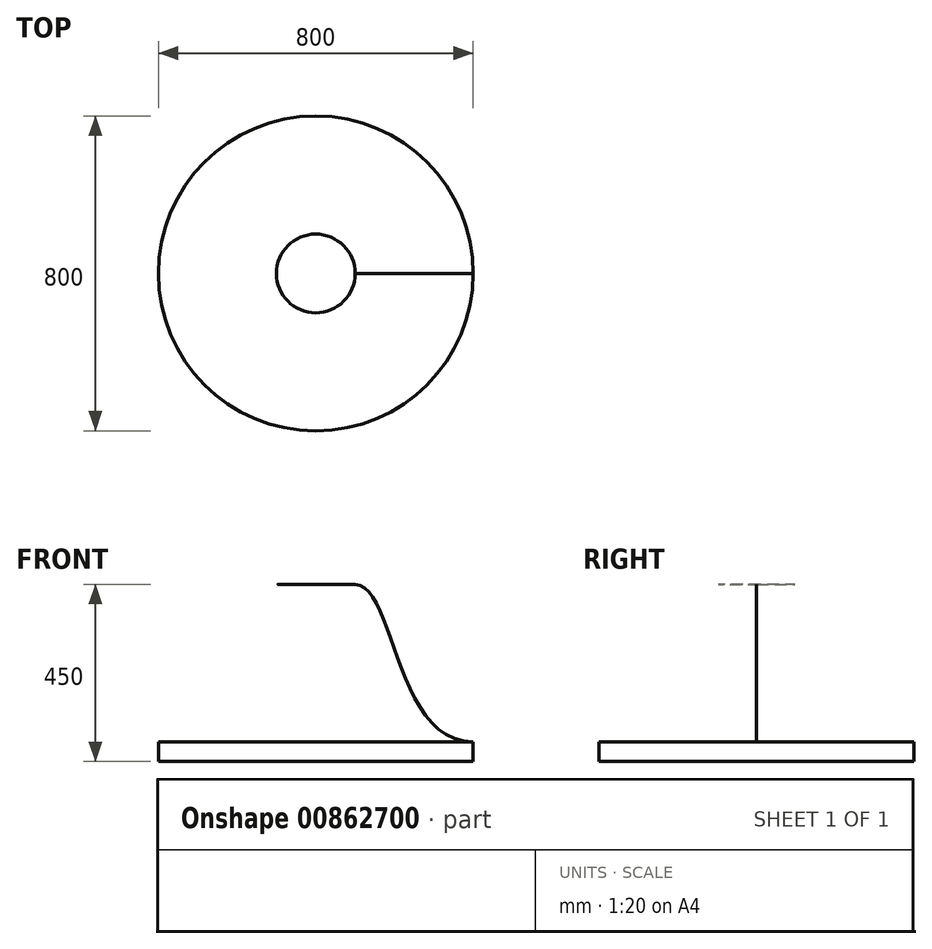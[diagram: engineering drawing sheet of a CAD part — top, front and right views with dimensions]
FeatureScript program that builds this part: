
annotation { "Feature Type Name" : "Feature", "Feature Type Description" : "" }
export const myFeature = defineFeature(function(context is Context, id is Id, definition is map)
    precondition{}
    {
        {
            var Q0;
            Q0=qCreatedBy(makeId("Top.planeOp"),FACE);
            var sketch = newSketch(context, id + "F0", { "sketchPlane" : qUnion([Q0])});
            skCircle(sketch, "E0", {"center": v(0, 0) * mm, "radius": 400 * mm});
            skSolve(sketch);
        }
        {
            var Q0;
            Q0=makeQuery(id+"F0.imprint","IMPRINT",FACE,{"disambiguationData":[TD([[makeQuery(id+"F0.imprint","IMPRINT",EDGE,{"derivedFrom":sQuery(id+"F0.wireOp",EDGE,"E0")}),1.0]])]});
            cPlane(context, id + "F1", {"entities" : qUnion([Q0]), "cplaneType" : CPlaneType.OFFSET, "offset" : 400 * mm, "width" : 150 * mm, "height" : 150 * mm});
        }
        {
            var Q0;
            Q0=qCreatedBy(id+"F1.planeOp",FACE);
            var sketch = newSketch(context, id + "F2", { "sketchPlane" : qUnion([Q0])});
            skCircle(sketch, "E1", {"center": v(0, 0) * mm, "radius": 100 * mm});
            skSolve(sketch);
        }
        {
            var Q0;
            Q0=makeQuery(id+"F0.imprint","IMPRINT",FACE,{"disambiguationData":[TD([[makeQuery(id+"F0.imprint","IMPRINT",EDGE,{"derivedFrom":sQuery(id+"F0.wireOp",EDGE,"E0")}),1.0]])]});
            var Q1;
            Q1=makeQuery(id+"F2.imprint","IMPRINT",FACE,{"disambiguationData":[TD([[makeQuery(id+"F2.imprint","IMPRINT",EDGE,{"derivedFrom":sQuery(id+"F2.wireOp",EDGE,"E1")}),1.0]])]});
            loft(context, id + "F3", {"startCondition" : LoftEndDerivativeType.TANGENT_TO_PROFILE, "startMagnitude" : 2, "endCondition" : LoftEndDerivativeType.TANGENT_TO_PROFILE, "endMagnitude" : 1, "sheetProfilesArray" : [{ "sheetProfileEntities" : qUnion([Q0]) }, { "sheetProfileEntities" : qUnion([Q1]) }]});
        }
        {
            var Q0;
            Q0=makeQuery(id+"F3.opLoft","CAP_FACE",FACE,{"disambiguationData":[OSD([makeQuery(id+"F0.imprint","IMPRINT",FACE,{"disambiguationData":[TD([[makeQuery(id+"F0.imprint","IMPRINT",EDGE,{"derivedFrom":sQuery(id+"F0.wireOp",EDGE,"E0")}),1.0]])]})])],"isStart":true});
            extrude(context, id + "F4", {"entities" : qUnion([Q0]), "operationType" : NewBodyOperationType.ADD, "depth" : 50 * mm, "offsetDistance" : 25 * mm});
        }
        {
            var Q0;
            Q0=makeQuery(id+"F0.imprint","IMPRINT",FACE,{"disambiguationData":[TD([[makeQuery(id+"F0.imprint","IMPRINT",EDGE,{"derivedFrom":sQuery(id+"F0.wireOp",EDGE,"E0")}),1.0]])]});
            cPlane(context, id + "F5", {"entities" : qUnion([Q0]), "cplaneType" : CPlaneType.OFFSET, "offset" : 400 * mm, "width" : 150 * mm, "height" : 150 * mm});
        }
    });
